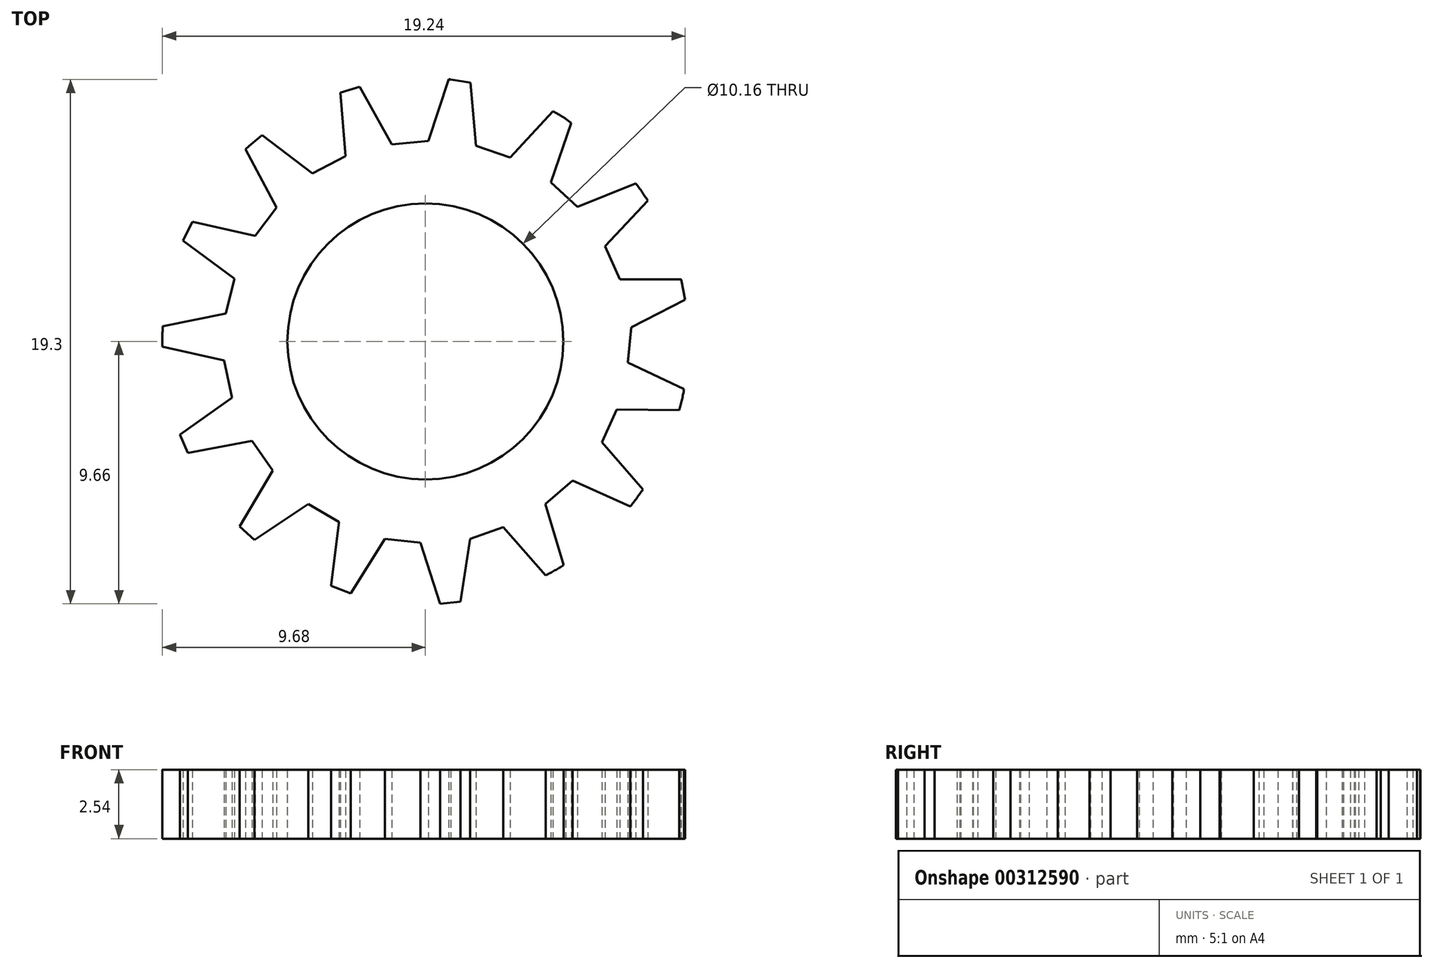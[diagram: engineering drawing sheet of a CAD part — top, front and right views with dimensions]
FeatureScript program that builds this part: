
annotation { "Feature Type Name" : "Feature", "Feature Type Description" : "" }
export const myFeature = defineFeature(function(context is Context, id is Id, definition is map)
    precondition{}
    {
        {
            var Q0;
            Q0=qCreatedBy(makeId("Top.planeOp"),FACE);
            var sketch = newSketch(context, id + "F0", { "sketchPlane" : qUnion([Q0])});
            skLineSegment(sketch, "E0", {"start": v(-6.3, -7.3) * mm, "end": v(-6.83, -6.82) * mm});
            skLineSegment(sketch, "E1", {"start": v(-5.62, -4.76) * mm, "end": v(-6.39, -3.67) * mm});
            skLineSegment(sketch, "E2", {"start": v(-6.39, -3.67) * mm, "end": v(-8.74, -4.1) * mm});
            skLineSegment(sketch, "E3", {"start": v(-9.03, -3.44) * mm, "end": v(-7.12, -2.07) * mm});
            skLineSegment(sketch, "E4", {"start": v(-7.12, -2.07) * mm, "end": v(-7.4, -0.7) * mm});
            skLineSegment(sketch, "E5", {"start": v(-7.03, 2.31) * mm, "end": v(-8.92, 3.7) * mm});
            skLineSegment(sketch, "E6", {"start": v(-8.92, 3.7) * mm, "end": v(-8.58, 4.4) * mm});
            skLineSegment(sketch, "E7", {"start": v(-8.58, 4.4) * mm, "end": v(-6.26, 3.88) * mm});
            skLineSegment(sketch, "E8", {"start": v(-6.26, 3.88) * mm, "end": v(-5.47, 4.93) * mm});
            skLineSegment(sketch, "E9", {"start": v(-5.47, 4.93) * mm, "end": v(-6.62, 7.08) * mm});
            skLineSegment(sketch, "E10", {"start": v(-6.62, 7.08) * mm, "end": v(-6.02, 7.6) * mm});
            skLineSegment(sketch, "E11", {"start": v(-6.02, 7.6) * mm, "end": v(-4.16, 6.18) * mm});
            skLineSegment(sketch, "E12", {"start": v(-4.16, 6.18) * mm, "end": v(-2.94, 6.81) * mm});
            skLineSegment(sketch, "E13", {"start": v(-3.13, 9.15) * mm, "end": v(-2.42, 9.37) * mm});
            skLineSegment(sketch, "E14", {"start": v(-2.42, 9.37) * mm, "end": v(-1.23, 7.25) * mm});
            skLineSegment(sketch, "E15", {"start": v(-1.23, 7.25) * mm, "end": v(0.11, 7.37) * mm});
            skLineSegment(sketch, "E16", {"start": v(0.11, 7.37) * mm, "end": v(0.85, 9.65) * mm});
            skLineSegment(sketch, "E17", {"start": v(0.85, 9.65) * mm, "end": v(1.66, 9.52) * mm});
            skLineSegment(sketch, "E18", {"start": v(1.66, 9.52) * mm, "end": v(1.86, 7.2) * mm});
            skLineSegment(sketch, "E19", {"start": v(1.86, 7.2) * mm, "end": v(3.12, 6.77) * mm});
            skLineSegment(sketch, "E20", {"start": v(3.12, 6.77) * mm, "end": v(4.73, 8.52) * mm});
            skLineSegment(sketch, "E21", {"start": v(4.73, 8.52) * mm, "end": v(5.37, 8.03) * mm});
            skLineSegment(sketch, "E22", {"start": v(7.82, 5.85) * mm, "end": v(8.23, 5.23) * mm});
            skLineSegment(sketch, "E23", {"start": v(7.15, 2.28) * mm, "end": v(9.41, 2.28) * mm});
            skLineSegment(sketch, "E24", {"start": v(9.41, 1.46) * mm, "end": v(7.57, 0.52) * mm});
            skLineSegment(sketch, "E25", {"start": v(7.57, 0.52) * mm, "end": v(7.45, -0.78) * mm});
            skLineSegment(sketch, "E26", {"start": v(7.45, -0.78) * mm, "end": v(9.61, -1.8) * mm});
            skLineSegment(sketch, "E27", {"start": v(9.61, -1.8) * mm, "end": v(9.44, -2.53) * mm});
            skLineSegment(sketch, "E28", {"start": v(9.44, -2.53) * mm, "end": v(7.05, -2.5) * mm});
            skLineSegment(sketch, "E29", {"start": v(7.05, -2.5) * mm, "end": v(6.5, -3.7) * mm});
            skLineSegment(sketch, "E30", {"start": v(6.5, -3.7) * mm, "end": v(8.05, -5.5) * mm});
            skLineSegment(sketch, "E31", {"start": v(8.05, -5.5) * mm, "end": v(7.6, -6.1) * mm});
            skLineSegment(sketch, "E32", {"start": v(7.6, -6.1) * mm, "end": v(5.42, -5.12) * mm});
            skLineSegment(sketch, "E33", {"start": v(5.42, -5.12) * mm, "end": v(4.41, -5.99) * mm});
            skLineSegment(sketch, "E34", {"start": v(4.41, -5.99) * mm, "end": v(5.1, -8.26) * mm});
            skLineSegment(sketch, "E35", {"start": v(5.1, -8.26) * mm, "end": v(4.44, -8.63) * mm});
            skLineSegment(sketch, "E36", {"start": v(4.44, -8.63) * mm, "end": v(2.86, -6.84) * mm});
            skLineSegment(sketch, "E37", {"start": v(2.86, -6.84) * mm, "end": v(1.64, -7.27) * mm});
            skLineSegment(sketch, "E38", {"start": v(1.64, -7.27) * mm, "end": v(1.28, -9.59) * mm});
            skLineSegment(sketch, "E39", {"start": v(1.28, -9.59) * mm, "end": v(0.54, -9.66) * mm});
            skLineSegment(sketch, "E40", {"start": v(0.54, -9.66) * mm, "end": v(-0.18, -7.4) * mm});
            skLineSegment(sketch, "E41", {"start": v(-0.18, -7.4) * mm, "end": v(-1.5, -7.27) * mm});
            skLineSegment(sketch, "E42", {"start": v(-1.5, -7.27) * mm, "end": v(-2.75, -9.27) * mm});
            skLineSegment(sketch, "E43", {"start": v(-2.75, -9.27) * mm, "end": v(-3.47, -9) * mm});
            skLineSegment(sketch, "E44", {"start": v(-3.47, -9) * mm, "end": v(-3.18, -6.65) * mm});
            skLineSegment(sketch, "E45", {"start": v(-3.18, -6.65) * mm, "end": v(-4.32, -6) * mm});
            skLineSegment(sketch, "E46", {"start": v(-4.32, -6) * mm, "end": v(-6.3, -7.3) * mm});
            skPoint(sketch, "E47.endSnap0", {"position": v(-6.57, -7.06) * mm});
            skLineSegment(sketch, "E48", {"start": v(-5.62, -4.76) * mm, "end": v(-6.83, -6.82) * mm});
            skLineSegment(sketch, "E49", {"start": v(-7.03, 2.31) * mm, "end": v(-7.34, 1.02) * mm});
            skLineSegment(sketch, "E50", {"start": v(-7.34, 1.02) * mm, "end": v(-9.7, 0.55) * mm});
            skLineSegment(sketch, "E51", {"start": v(-9.7, 0.55) * mm, "end": v(-9.7, -0.2) * mm});
            skLineSegment(sketch, "E52", {"start": v(-9.7, -0.2) * mm, "end": v(-7.4, -0.7) * mm});
            skLineSegment(sketch, "E53", {"start": v(-2.94, 6.81) * mm, "end": v(-3.13, 9.15) * mm});
            skLineSegment(sketch, "E54", {"start": v(5.37, 8.03) * mm, "end": v(4.62, 5.85) * mm});
            skLineSegment(sketch, "E55", {"start": v(4.62, 5.85) * mm, "end": v(5.6, 4.95) * mm});
            skLineSegment(sketch, "E56", {"start": v(5.6, 4.95) * mm, "end": v(7.82, 5.85) * mm});
            skLineSegment(sketch, "E57", {"start": v(8.23, 5.23) * mm, "end": v(6.61, 3.5) * mm});
            skLineSegment(sketch, "E58", {"start": v(6.61, 3.5) * mm, "end": v(7.15, 2.28) * mm});
            skLineSegment(sketch, "E59", {"start": v(-8.74, -4.1) * mm, "end": v(-9.03, -3.44) * mm});
            skLineSegment(sketch, "E60", {"start": v(5.42, -5.12) * mm, "end": v(7.6, -6.1) * mm});
            skCircle(sketch, "E61", {"center": v(0, 0) * mm, "radius": 9.68 * mm});
            skLineSegment(sketch, "E62", {"start": v(7.57, 0.52) * mm, "end": v(9.56, 1.54) * mm});
            skLineSegment(sketch, "E63", {"start": v(9.56, 1.54) * mm, "end": v(9.41, 2.28) * mm});
            skSolve(sketch);
        }
        {
            var Q0;
            Q0=makeQuery(id+"F0.imprint","IMPRINT",FACE,{"disambiguationData":[TD([[makeQuery(id+"F0.imprint","IMPRINT",EDGE,{"derivedFrom":sQuery(id+"F0.wireOp",EDGE,"E0")}),-1.0]])]});
            extrude(context, id + "F1", {"entities" : qUnion([Q0]), "depth" : 2.54 * mm});
        }
        {
            var Q0;
            Q0=makeQuery(id+"F1.opExtrude","CAP_FACE",FACE,{"disambiguationData":[OSD([sQuery(id+"F0.wireOp",EDGE,"E0"),sQuery(id+"F0.wireOp",EDGE,"E1"),sQuery(id+"F0.wireOp",EDGE,"E2"),sQuery(id+"F0.wireOp",EDGE,"E3"),sQuery(id+"F0.wireOp",EDGE,"E4"),sQuery(id+"F0.wireOp",EDGE,"E5"),sQuery(id+"F0.wireOp",EDGE,"E6"),sQuery(id+"F0.wireOp",EDGE,"E7"),sQuery(id+"F0.wireOp",EDGE,"E8"),sQuery(id+"F0.wireOp",EDGE,"E9"),sQuery(id+"F0.wireOp",EDGE,"E11"),sQuery(id+"F0.wireOp",EDGE,"E12"),sQuery(id+"F0.wireOp",EDGE,"E13"),sQuery(id+"F0.wireOp",EDGE,"E14"),sQuery(id+"F0.wireOp",EDGE,"E15"),sQuery(id+"F0.wireOp",EDGE,"E16"),sQuery(id+"F0.wireOp",EDGE,"E17"),sQuery(id+"F0.wireOp",EDGE,"E18"),sQuery(id+"F0.wireOp",EDGE,"E19"),sQuery(id+"F0.wireOp",EDGE,"E20"),sQuery(id+"F0.wireOp",EDGE,"E21"),sQuery(id+"F0.wireOp",EDGE,"E23"),sQuery(id+"F0.wireOp",EDGE,"E25"),sQuery(id+"F0.wireOp",EDGE,"E26"),sQuery(id+"F0.wireOp",EDGE,"E28"),sQuery(id+"F0.wireOp",EDGE,"E29"),sQuery(id+"F0.wireOp",EDGE,"E30"),sQuery(id+"F0.wireOp",EDGE,"E33"),sQuery(id+"F0.wireOp",EDGE,"E34"),sQuery(id+"F0.wireOp",EDGE,"E36"),sQuery(id+"F0.wireOp",EDGE,"E37"),sQuery(id+"F0.wireOp",EDGE,"E38"),sQuery(id+"F0.wireOp",EDGE,"E39"),sQuery(id+"F0.wireOp",EDGE,"E40"),sQuery(id+"F0.wireOp",EDGE,"E41"),sQuery(id+"F0.wireOp",EDGE,"E42"),sQuery(id+"F0.wireOp",EDGE,"E43"),sQuery(id+"F0.wireOp",EDGE,"E44"),sQuery(id+"F0.wireOp",EDGE,"E45"),sQuery(id+"F0.wireOp",EDGE,"E46"),sQuery(id+"F0.wireOp",EDGE,"E48"),sQuery(id+"F0.wireOp",EDGE,"E49"),sQuery(id+"F0.wireOp",EDGE,"E50"),sQuery(id+"F0.wireOp",EDGE,"E52"),sQuery(id+"F0.wireOp",EDGE,"E53"),sQuery(id+"F0.wireOp",EDGE,"E54"),sQuery(id+"F0.wireOp",EDGE,"E55"),sQuery(id+"F0.wireOp",EDGE,"E56"),sQuery(id+"F0.wireOp",EDGE,"E57"),sQuery(id+"F0.wireOp",EDGE,"E58"),sQuery(id+"F0.wireOp",EDGE,"E59"),sQuery(id+"F0.wireOp",EDGE,"E60"),sQuery(id+"F0.wireOp",EDGE,"E61"),sQuery(id+"F0.wireOp",EDGE,"E62"),sQuery(id+"F0.wireOp",EDGE,"E63")])],"isStart":false});
            var sketch = newSketch(context, id + "F2", { "sketchPlane" : qUnion([Q0])});
            skSolve(sketch);
        }
        {
            var Q0;
            Q0=makeQuery(id+"F1.opExtrude","SWEPT_BODY",BODY,{"disambiguationData":[OSD([sQuery(id+"F0.wireOp",EDGE,"E0"),sQuery(id+"F0.wireOp",EDGE,"E1"),sQuery(id+"F0.wireOp",EDGE,"E2"),sQuery(id+"F0.wireOp",EDGE,"E3"),sQuery(id+"F0.wireOp",EDGE,"E4"),sQuery(id+"F0.wireOp",EDGE,"E5"),sQuery(id+"F0.wireOp",EDGE,"E6"),sQuery(id+"F0.wireOp",EDGE,"E7"),sQuery(id+"F0.wireOp",EDGE,"E8"),sQuery(id+"F0.wireOp",EDGE,"E9"),sQuery(id+"F0.wireOp",EDGE,"E11"),sQuery(id+"F0.wireOp",EDGE,"E12"),sQuery(id+"F0.wireOp",EDGE,"E13"),sQuery(id+"F0.wireOp",EDGE,"E14"),sQuery(id+"F0.wireOp",EDGE,"E15"),sQuery(id+"F0.wireOp",EDGE,"E16"),sQuery(id+"F0.wireOp",EDGE,"E17"),sQuery(id+"F0.wireOp",EDGE,"E18"),sQuery(id+"F0.wireOp",EDGE,"E19"),sQuery(id+"F0.wireOp",EDGE,"E20"),sQuery(id+"F0.wireOp",EDGE,"E21"),sQuery(id+"F0.wireOp",EDGE,"E23"),sQuery(id+"F0.wireOp",EDGE,"E25"),sQuery(id+"F0.wireOp",EDGE,"E26"),sQuery(id+"F0.wireOp",EDGE,"E28"),sQuery(id+"F0.wireOp",EDGE,"E29"),sQuery(id+"F0.wireOp",EDGE,"E30"),sQuery(id+"F0.wireOp",EDGE,"E33"),sQuery(id+"F0.wireOp",EDGE,"E34"),sQuery(id+"F0.wireOp",EDGE,"E36"),sQuery(id+"F0.wireOp",EDGE,"E37"),sQuery(id+"F0.wireOp",EDGE,"E38"),sQuery(id+"F0.wireOp",EDGE,"E39"),sQuery(id+"F0.wireOp",EDGE,"E40"),sQuery(id+"F0.wireOp",EDGE,"E41"),sQuery(id+"F0.wireOp",EDGE,"E42"),sQuery(id+"F0.wireOp",EDGE,"E43"),sQuery(id+"F0.wireOp",EDGE,"E44"),sQuery(id+"F0.wireOp",EDGE,"E45"),sQuery(id+"F0.wireOp",EDGE,"E46"),sQuery(id+"F0.wireOp",EDGE,"E48"),sQuery(id+"F0.wireOp",EDGE,"E49"),sQuery(id+"F0.wireOp",EDGE,"E50"),sQuery(id+"F0.wireOp",EDGE,"E52"),sQuery(id+"F0.wireOp",EDGE,"E53"),sQuery(id+"F0.wireOp",EDGE,"E54"),sQuery(id+"F0.wireOp",EDGE,"E55"),sQuery(id+"F0.wireOp",EDGE,"E56"),sQuery(id+"F0.wireOp",EDGE,"E57"),sQuery(id+"F0.wireOp",EDGE,"E58"),sQuery(id+"F0.wireOp",EDGE,"E59"),sQuery(id+"F0.wireOp",EDGE,"E60"),sQuery(id+"F0.wireOp",EDGE,"E61"),sQuery(id+"F0.wireOp",EDGE,"E62"),sQuery(id+"F0.wireOp",EDGE,"E63")])]});
            var Q1;
            Q1=sQuery(id+"F0.wireOp",VERTEX,"E61.center");
            transform(context, id + "F3", {"entities" : qUnion([Q0]), "transformType" : TransformType.SCALE_UNIFORMLY, "scale" : 1, "scalePoint" : qUnion([Q1]), "makeCopy" : false});
        }
        {
            var Q0;
            Q0=sQuery(id+"F0.wireOp",VERTEX,"E61.center");
            var Q1;
            Q1=makeQuery(id+"F1.opExtrude","SWEPT_BODY",BODY,{"disambiguationData":[OSD([sQuery(id+"F0.wireOp",EDGE,"E0"),sQuery(id+"F0.wireOp",EDGE,"E1"),sQuery(id+"F0.wireOp",EDGE,"E2"),sQuery(id+"F0.wireOp",EDGE,"E3"),sQuery(id+"F0.wireOp",EDGE,"E4"),sQuery(id+"F0.wireOp",EDGE,"E5"),sQuery(id+"F0.wireOp",EDGE,"E6"),sQuery(id+"F0.wireOp",EDGE,"E7"),sQuery(id+"F0.wireOp",EDGE,"E8"),sQuery(id+"F0.wireOp",EDGE,"E9"),sQuery(id+"F0.wireOp",EDGE,"E11"),sQuery(id+"F0.wireOp",EDGE,"E12"),sQuery(id+"F0.wireOp",EDGE,"E13"),sQuery(id+"F0.wireOp",EDGE,"E14"),sQuery(id+"F0.wireOp",EDGE,"E15"),sQuery(id+"F0.wireOp",EDGE,"E16"),sQuery(id+"F0.wireOp",EDGE,"E17"),sQuery(id+"F0.wireOp",EDGE,"E18"),sQuery(id+"F0.wireOp",EDGE,"E19"),sQuery(id+"F0.wireOp",EDGE,"E20"),sQuery(id+"F0.wireOp",EDGE,"E21"),sQuery(id+"F0.wireOp",EDGE,"E23"),sQuery(id+"F0.wireOp",EDGE,"E25"),sQuery(id+"F0.wireOp",EDGE,"E26"),sQuery(id+"F0.wireOp",EDGE,"E28"),sQuery(id+"F0.wireOp",EDGE,"E29"),sQuery(id+"F0.wireOp",EDGE,"E30"),sQuery(id+"F0.wireOp",EDGE,"E33"),sQuery(id+"F0.wireOp",EDGE,"E34"),sQuery(id+"F0.wireOp",EDGE,"E36"),sQuery(id+"F0.wireOp",EDGE,"E37"),sQuery(id+"F0.wireOp",EDGE,"E38"),sQuery(id+"F0.wireOp",EDGE,"E39"),sQuery(id+"F0.wireOp",EDGE,"E40"),sQuery(id+"F0.wireOp",EDGE,"E41"),sQuery(id+"F0.wireOp",EDGE,"E42"),sQuery(id+"F0.wireOp",EDGE,"E43"),sQuery(id+"F0.wireOp",EDGE,"E44"),sQuery(id+"F0.wireOp",EDGE,"E45"),sQuery(id+"F0.wireOp",EDGE,"E46"),sQuery(id+"F0.wireOp",EDGE,"E48"),sQuery(id+"F0.wireOp",EDGE,"E49"),sQuery(id+"F0.wireOp",EDGE,"E50"),sQuery(id+"F0.wireOp",EDGE,"E52"),sQuery(id+"F0.wireOp",EDGE,"E53"),sQuery(id+"F0.wireOp",EDGE,"E54"),sQuery(id+"F0.wireOp",EDGE,"E55"),sQuery(id+"F0.wireOp",EDGE,"E56"),sQuery(id+"F0.wireOp",EDGE,"E57"),sQuery(id+"F0.wireOp",EDGE,"E58"),sQuery(id+"F0.wireOp",EDGE,"E59"),sQuery(id+"F0.wireOp",EDGE,"E60"),sQuery(id+"F0.wireOp",EDGE,"E61"),sQuery(id+"F0.wireOp",EDGE,"E62"),sQuery(id+"F0.wireOp",EDGE,"E63")])]});
            hole(context, id + "F4", {"style" : HoleStyle.SIMPLE, "endStyle" : HoleEndStyle.BLIND, "oppositeDirection" : true, "holeDiameter" : 10.16 * mm, "holeDepth" : 2.54 * mm, "tappedDepth" : 12.7 * mm, "tapClearance" : 3, "locations" : qUnion([Q0]), "scope" : qUnion([Q1])});
        }
    });
